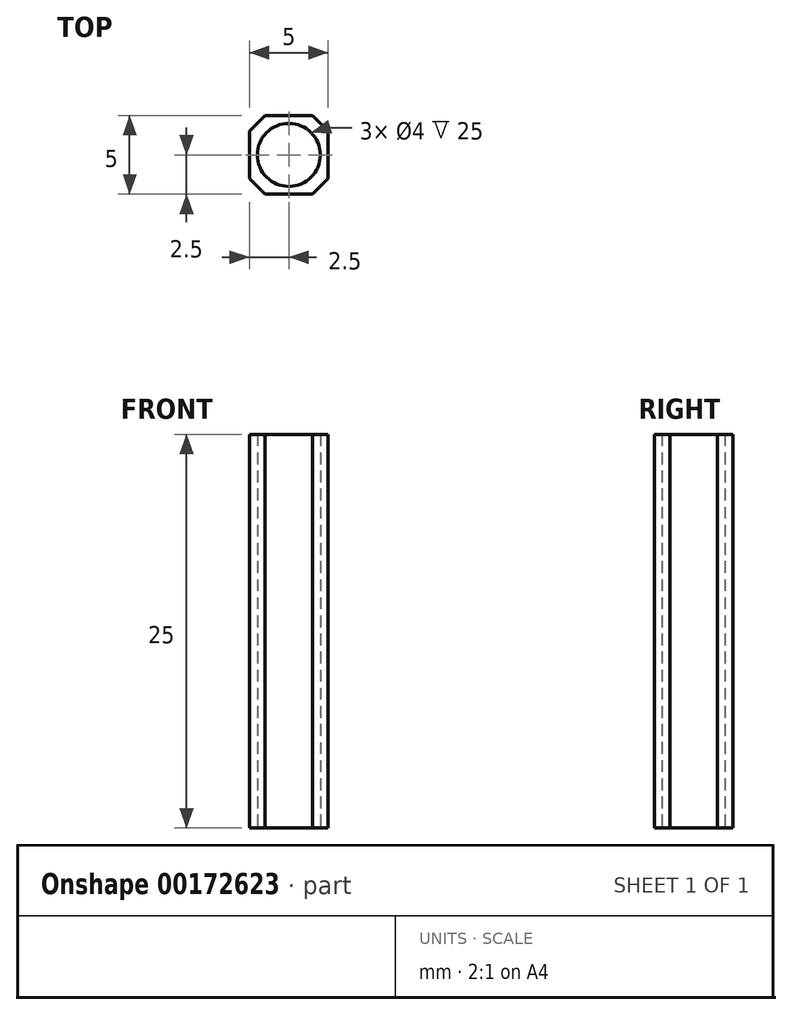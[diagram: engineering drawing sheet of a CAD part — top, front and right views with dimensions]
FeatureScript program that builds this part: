
annotation { "Feature Type Name" : "Feature", "Feature Type Description" : "" }
export const myFeature = defineFeature(function(context is Context, id is Id, definition is map)
    precondition{}
    {
        {
            var Q0;
            Q0=qCreatedBy(makeId("Top.planeOp"),FACE);
            var sketch = newSketch(context, id + "F0", { "sketchPlane" : qUnion([Q0])});
            skLineSegment(sketch, "E0.bottom", {"start": v(-1.5, 2.5) * mm, "end": v(1.5, 2.5) * mm});
            skLineSegment(sketch, "E0.top", {"start": v(-1.5, -2.5) * mm, "end": v(1.5, -2.5) * mm});
            skLineSegment(sketch, "E0.left", {"start": v(-2.5, 1.5) * mm, "end": v(-2.5, -1.5) * mm});
            skLineSegment(sketch, "E0.right", {"start": v(2.5, 1.5) * mm, "end": v(2.5, -1.5) * mm});
            skPoint(sketch, "E0.middle", {"position": v(0, 0) * mm});
            skPoint(sketch, "E1", {"position": v(0, 2.5) * mm});
            skPoint(sketch, "E2", {"position": v(2.5, 0) * mm});
            skPoint(sketch, "E3", {"position": v(0, -2.5) * mm});
            skPoint(sketch, "E4", {"position": v(-2.5, 0) * mm});
            skPoint(sketch, "E5", {"position": v(-2.5, 1.5) * mm});
            skPoint(sketch, "E6", {"position": v(-1.5, 2.5) * mm});
            skPoint(sketch, "E7", {"position": v(2.5, 1.5) * mm});
            skPoint(sketch, "E8", {"position": v(1.5, -2.5) * mm});
            skPoint(sketch, "E9.MirrorP", {"position": v(-2.5, -1.5) * mm});
            skPoint(sketch, "E10.MirrorP", {"position": v(2.5, -1.5) * mm});
            skPoint(sketch, "E11.MirrorP", {"position": v(1.5, 2.5) * mm});
            skPoint(sketch, "E12.MirrorP", {"position": v(-1.5, -2.5) * mm});
            skLineSegment(sketch, "E13", {"start": v(-2.5, 1.5) * mm, "end": v(-1.5, 2.5) * mm});
            skLineSegment(sketch, "E14", {"start": v(1.5, 2.5) * mm, "end": v(2.5, 1.5) * mm});
            skLineSegment(sketch, "E15", {"start": v(2.5, -1.5) * mm, "end": v(1.5, -2.5) * mm});
            skLineSegment(sketch, "E16", {"start": v(-2.5, -1.5) * mm, "end": v(-1.5, -2.5) * mm});
            skCircle(sketch, "E17", {"center": v(0, 0) * mm, "radius": 2 * mm});
            skSolve(sketch);
        }
        {
            var Q0;
            Q0=makeQuery(id+"F0.imprint","IMPRINT",FACE,{"disambiguationData":[TD([[makeQuery(id+"F0.imprint","IMPRINT",EDGE,{"derivedFrom":sQuery(id+"F0.wireOp",EDGE,"E0.bottom")}),-1.0]])]});
            extrude(context, id + "F1", {"entities" : qUnion([Q0]), "depth" : 25 * mm});
        }
    });
